# Revit family: Faucet-Bobrick-Designer_Series-B-887X_Series
name_source: partatom
category: Plumbing Fixtures
revit_build: Autodesk Revit 2018 (Build: 20170223_1515(x64)
units: mm (PartAtom-declared; Revit-internal decimal feet)

## family parameters
Always vertical = No
Cut with Voids When Loaded = No
OmniClass Number = 23.45.55.14
OmniClass Title = Single Faucets
Part Type = Normal
Room Calculation Point = No
Round Connector Dimension = Use Diameter
Shared = Yes
Work Plane-Based = Yes

## types (5) — shared parameters
0.35 gpm (1.3 Lpm) Flow Rate = No
0.5 gpm (1.9 Lpm) Flow Rate (Standard) = Yes
1.0 gpm (3.8 Lpm) Flow Rate = No
1.5 gpm (5.7 Lpm) Flow Rate = No
2.2 gpm (8.3 Lpm) Flow Rate = No
4" (102 mm) Escutcheon Plate = No
8" (203 mm) Escutcheon Plate = No
ADA Compliant = Yes
Assembly Code = D2020300
CW Connection = Yes
CWFU = 1.5
Cold Water Connection Diameter = 3/8"
Cold Water Connection Radius = 3/16"
Default Elevation = 0"
Flow Control Option = 2
Flow Rate = 0.5 gpm (1.9 Lpm)
HW Connection = Yes
HWFU = 1.5
Height = 5 1/2"
Hot Water Connection Diameter = 0"
Hot Water Connection Radius = 3/16"
Installation Type = Deck Mounted
Length = 6 1/2"
Manufacturer = Bobrick Washroom Equipment, Inc.
Price = Prices may vary. Please consult Manufacturer Representative for most up-to-date price list.
Product Page URL = https://www.bobrick.com
URL = http://bobrick.com
Vent Connection = No
Warranty Information = 3 Year Limited Warranty
Waste Connection = No
Width = 2 3/4"
zero-valued in all types: WFU

## per-type parameters (varying)
| type | Description | Finish | Material | Specification |
| B-8878 | Designer Series Automatic, Battery-powered , Polished Chrome Lavatory Faucet | Die-Cast Zinc-Bobrick-Polished Chrome | Die-Cast Zinc-Bobrick-Polished Chrome | Deck-Mounted, Automatic, Electric-Sensor Operated Lavatory Faucet B-8878 shall be polished chrome die-cast zinc. Hot and cold water indicators shall be included; coordinate faucet inlets with supplies and fixture hole punching, coordinate outlet with spout and fixture receptor. Unit shall have a hidden infrared convergence-type proximity sensor lens. Spout assembly shall be polished chrome plated with integral shank to accommodate up to 2" (50mm) thick counter tops. Automatic Soap Dispenser available with matching Polished Chrome Finish: B-848 (Foam) or B-858 (Liquid). |
| B-8875 | Designer Series Automatic, Battery-powered , Brushed Nickel Lavatory Faucet | Die-Cast Zinc-Bobrick-Brushed Nickel | Die-Cast Zinc-Bobrick-Brushed Nickel | Deck-Mounted, Automatic, Electric-Sensor Operated Lavatory Faucet B-8875 shall be brushed nickel die-cast zinc. Hot and cold water indicators shall be included; coordinate faucet inlets with supplies and fixture hole punching, coordinate outlet with spout and fixture receptor. Unit shall have a hidden infrared convergence-type proximity sensor lens. Spout assembly shall be polished chrome plated with integral shank to accommodate up to 2" (50mm) thick counter tops. Automatic Soap Dispenser available with matching Brushed Nickel Finish: B-845 (Foam) or B-855 (Liquid). |
| B-8876 | Designer Series Automatic, Battery-powered , Polished Nickel Lavatory Faucet | Die-Cast Zinc-Bobrick-Polished Nickel | Die-Cast Zinc-Bobrick-Polished Nickel | Deck-Mounted, Automatic, Electric-Sensor Operated Lavatory Faucet B-8876 shall be polished nickel die-cast zinc. Hot and cold water indicators shall be included; coordinate faucet inlets with supplies and fixture hole punching, coordinate outlet with spout and fixture receptor. Unit shall have a hidden infrared convergence-type proximity sensor lens. Spout assembly shall be polished chrome plated with integral shank to accommodate up to 2" (50mm) thick counter tops. Automatic Soap Dispenser available with matching Polished Nickel Finish: B-846 (Foam) or B-856 (Liquid). |
| B-8870 | Designer Series Automatic, Battery-powered , Polished Brass Lavatory Faucet | Die-Cast Zinc-Bobrick-Polished Brass | Die-Cast Zinc-Bobrick-Polished Brass | Deck-Mounted, Automatic, Electric-Sensor Operated Lavatory Faucet B-8870 shall be polished brass die-cast zinc. Hot and cold water indicators shall be included; coordinate faucet inlets with supplies and fixture hole punching, coordinate outlet with spout and fixture receptor. Unit shall have a hidden infrared convergence-type proximity sensor lens. Spout assembly shall be polished chrome plated with integral shank to accommodate up to 2" (50mm) thick counter tops. Automatic Soap Dispenser available with matching Polished Brass Finish: B-840 (Foam) or B-85o (Liquid). |
| B-8872 | Designer Series Automatic, Battery-powered , Polished Brass Lavatory Faucet | Die-Cast Zink-Bobrick-Matte Black | Die-Cast Zink-Bobrick-Matte Black | Deck-Mounted, Automatic, Electric-Sensor Operated Lavatory Faucet B-8870 shall be polished brass die-cast zinc. Hot and cold water indicators shall be included; coordinate faucet inlets with supplies and fixture hole punching, coordinate outlet with spout and fixture receptor. Unit shall have a hidden infrared convergence-type proximity sensor lens. Spout assembly shall be polished chrome plated with integral shank to accommodate up to 2" (50mm) thick counter tops. Automatic Soap Dispenser available with matching Polished Brass Finish: B-840 (Foam) or B-85o (Liquid). |

note: column(s) folded — value = type name in every type: Model

## geometry (parser evidence)
native form markers: Sweep x2
no freeform markers — native parametric forms only
